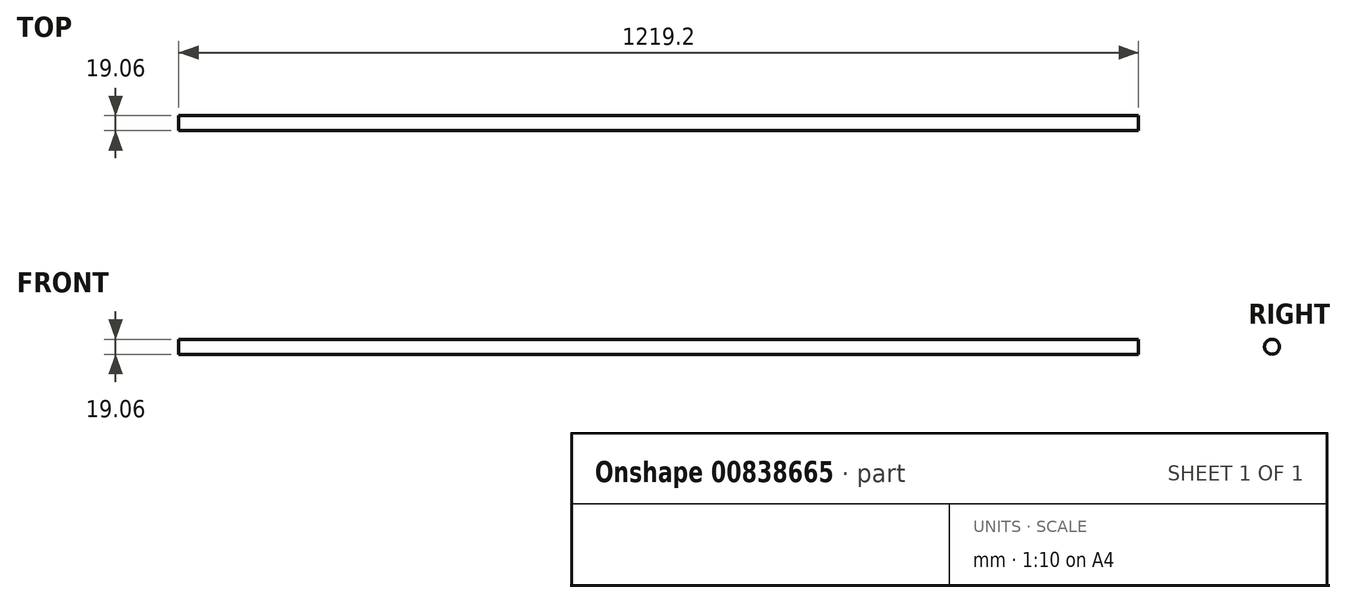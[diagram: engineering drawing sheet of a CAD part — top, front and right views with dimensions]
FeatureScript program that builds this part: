
annotation { "Feature Type Name" : "Feature", "Feature Type Description" : "" }
export const myFeature = defineFeature(function(context is Context, id is Id, definition is map)
    precondition{}
    {
        {
            var Q0;
            Q0=qCreatedBy(makeId("Right.planeOp"),FACE);
            var sketch = newSketch(context, id + "F0", { "sketchPlane" : qUnion([Q0])});
            skCircle(sketch, "E0", {"center": v(0, 0) * mm, "radius": 9.53 * mm});
            skSolve(sketch);
        }
        {
            var Q0;
            Q0 = qSketchRegion(id + "F0", true);
            extrude(context, id + "F1", {"entities" : qUnion([Q0]), "depth" : 1219.2 * mm, "offsetDistance" : 25.4 * mm, "symmetric" : true});
        }
    });
